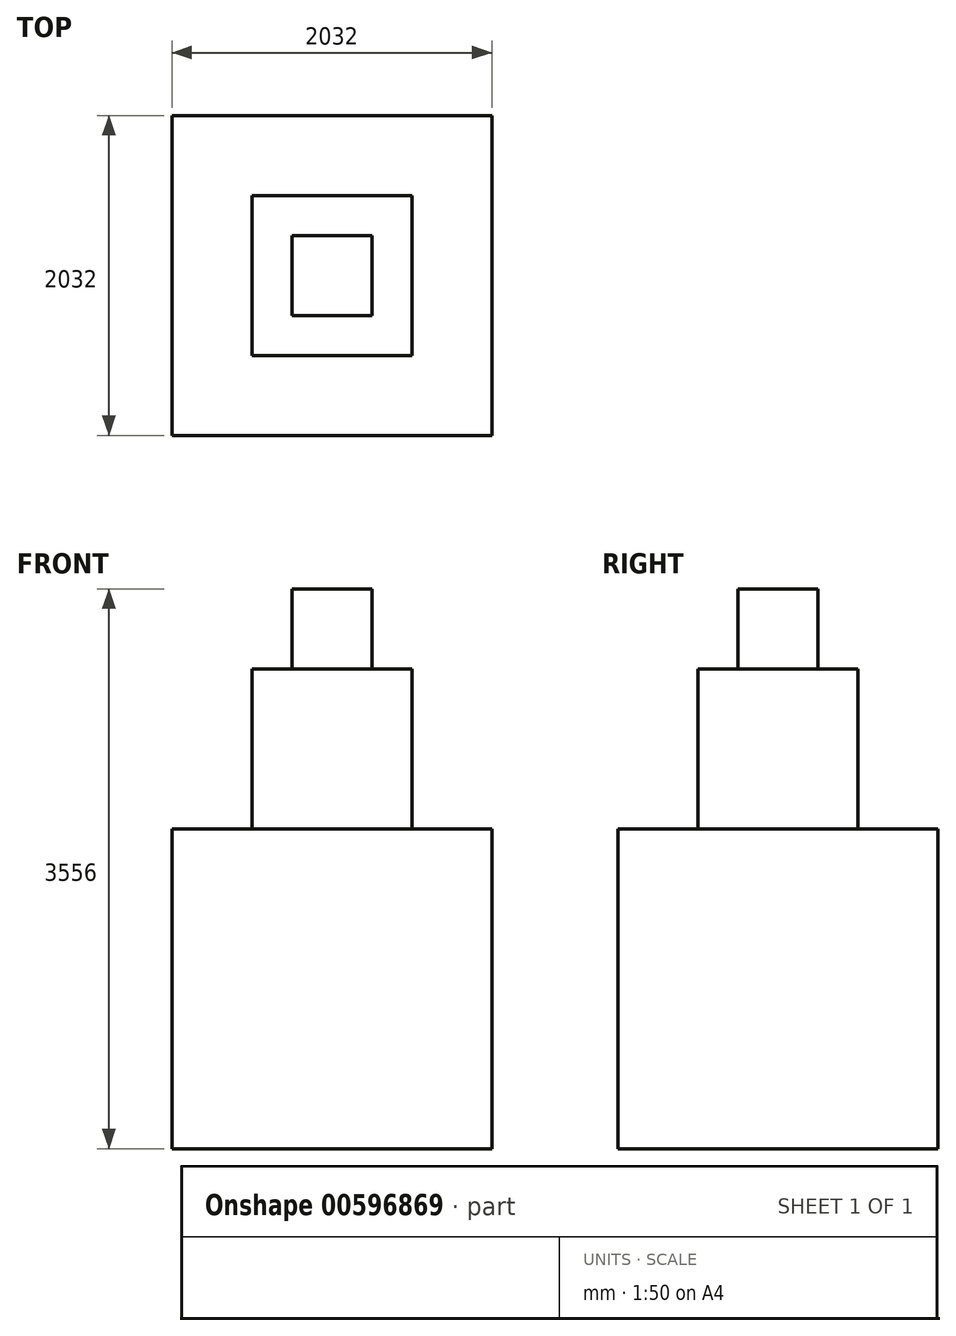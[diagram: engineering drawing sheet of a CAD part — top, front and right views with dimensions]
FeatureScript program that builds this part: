
annotation { "Feature Type Name" : "Feature", "Feature Type Description" : "" }
export const myFeature = defineFeature(function(context is Context, id is Id, definition is map)
    precondition{}
    {
        {
            var Q0;
            Q0=qCreatedBy(makeId("Right.planeOp"),FACE);
            var sketch = newSketch(context, id + "F0", { "sketchPlane" : qUnion([Q0])});
            skLineSegment(sketch, "E0.bottom", {"start": v(1016, 1016) * mm, "end": v(-1016, 1016) * mm});
            skLineSegment(sketch, "E0.top", {"start": v(1016, -1016) * mm, "end": v(-1016, -1016) * mm});
            skLineSegment(sketch, "E0.left", {"start": v(1016, 1016) * mm, "end": v(1016, -1016) * mm});
            skLineSegment(sketch, "E0.right", {"start": v(-1016, 1016) * mm, "end": v(-1016, -1016) * mm});
            skPoint(sketch, "E0.middle", {"position": v(0, 0) * mm});
            skSolve(sketch);
        }
        {
            var Q0;
            Q0=makeQuery(id+"F0.imprint","IMPRINT",FACE,{"disambiguationData":[TD([[makeQuery(id+"F0.imprint","IMPRINT",EDGE,{"derivedFrom":sQuery(id+"F0.wireOp",EDGE,"E0.bottom")}),1.0]])]});
            extrude(context, id + "F1", {"entities" : qUnion([Q0]), "depth" : 2032 * mm, "offsetDistance" : 25.4 * mm});
        }
        {
            var Q0;
            Q0=makeQuery(id+"F1.opExtrude","SWEPT_FACE",FACE,{"disambiguationData":[OSD([sQuery(id+"F0.wireOp",EDGE,"E0.bottom")])]});
            var sketch = newSketch(context, id + "F2", { "sketchPlane" : qUnion([Q0])});
            skLineSegment(sketch, "E1.bottom", {"start": v(508, 508) * mm, "end": v(1524, 508) * mm});
            skLineSegment(sketch, "E1.top", {"start": v(508, -508) * mm, "end": v(1524, -508) * mm});
            skLineSegment(sketch, "E1.left", {"start": v(508, 508) * mm, "end": v(508, -508) * mm});
            skLineSegment(sketch, "E1.right", {"start": v(1524, 508) * mm, "end": v(1524, -508) * mm});
            skSolve(sketch);
        }
        {
            var Q0;
            Q0=makeQuery(id+"F2.imprint","IMPRINT",FACE,{"disambiguationData":[TD([[makeQuery(id+"F2.imprint","IMPRINT",EDGE,{"derivedFrom":sQuery(id+"F2.wireOp",EDGE,"E1.bottom")}),-1.0]])]});
            extrude(context, id + "F3", {"entities" : qUnion([Q0]), "operationType" : NewBodyOperationType.ADD, "depth" : 1016 * mm, "offsetDistance" : 25.4 * mm});
        }
        {
            var Q0;
            Q0=makeQuery(id+"F3.opExtrude","CAP_FACE",FACE,{"disambiguationData":[OSD([sQuery(id+"F2.wireOp",EDGE,"E1.bottom"),sQuery(id+"F2.wireOp",EDGE,"E1.top"),sQuery(id+"F2.wireOp",EDGE,"E1.left"),sQuery(id+"F2.wireOp",EDGE,"E1.right")])],"isStart":false});
            var sketch = newSketch(context, id + "F4", { "sketchPlane" : qUnion([Q0])});
            skLineSegment(sketch, "E2.bottom", {"start": v(762, 254) * mm, "end": v(1270, 254) * mm});
            skLineSegment(sketch, "E2.top", {"start": v(762, -254) * mm, "end": v(1270, -254) * mm});
            skLineSegment(sketch, "E2.left", {"start": v(762, 254) * mm, "end": v(762, -254) * mm});
            skLineSegment(sketch, "E2.right", {"start": v(1270, 254) * mm, "end": v(1270, -254) * mm});
            skSolve(sketch);
        }
        {
            var Q0;
            Q0=makeQuery(id+"F4.imprint","IMPRINT",FACE,{"disambiguationData":[TD([[makeQuery(id+"F4.imprint","IMPRINT",EDGE,{"derivedFrom":sQuery(id+"F4.wireOp",EDGE,"E2.bottom")}),-1.0]])]});
            extrude(context, id + "F5", {"entities" : qUnion([Q0]), "operationType" : NewBodyOperationType.ADD, "depth" : 508 * mm, "offsetDistance" : 25.4 * mm});
        }
    });
